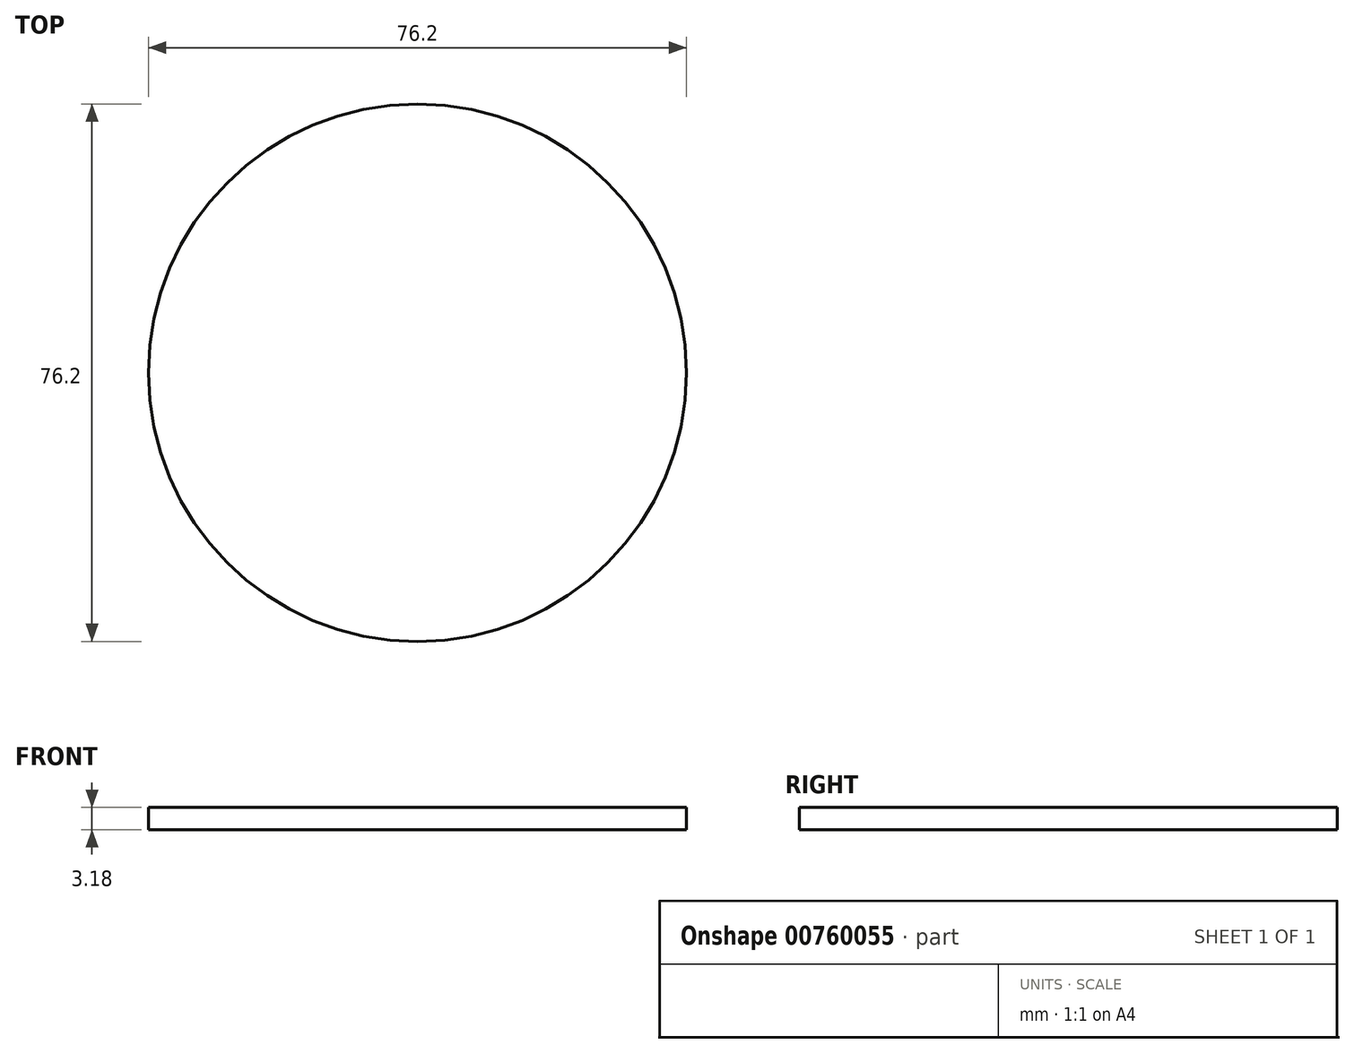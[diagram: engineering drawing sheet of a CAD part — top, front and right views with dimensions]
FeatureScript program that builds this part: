
annotation { "Feature Type Name" : "Feature", "Feature Type Description" : "" }
export const myFeature = defineFeature(function(context is Context, id is Id, definition is map)
    precondition{}
    {
        {
            var Q0;
            Q0=qCreatedBy(makeId("Top.planeOp"),FACE);
            var sketch = newSketch(context, id + "F0", { "sketchPlane" : qUnion([Q0])});
            skCircle(sketch, "E0", {"center": v(0, 0) * mm, "radius": 38.1 * mm});
            skSolve(sketch);
        }
        {
            var Q0;
            Q0 = qSketchRegion(id + "F0", true);
            extrude(context, id + "F1", {"entities" : qUnion([Q0]), "depth" : 3.17 * mm, "offsetDistance" : 25.4 * mm});
        }
    });
